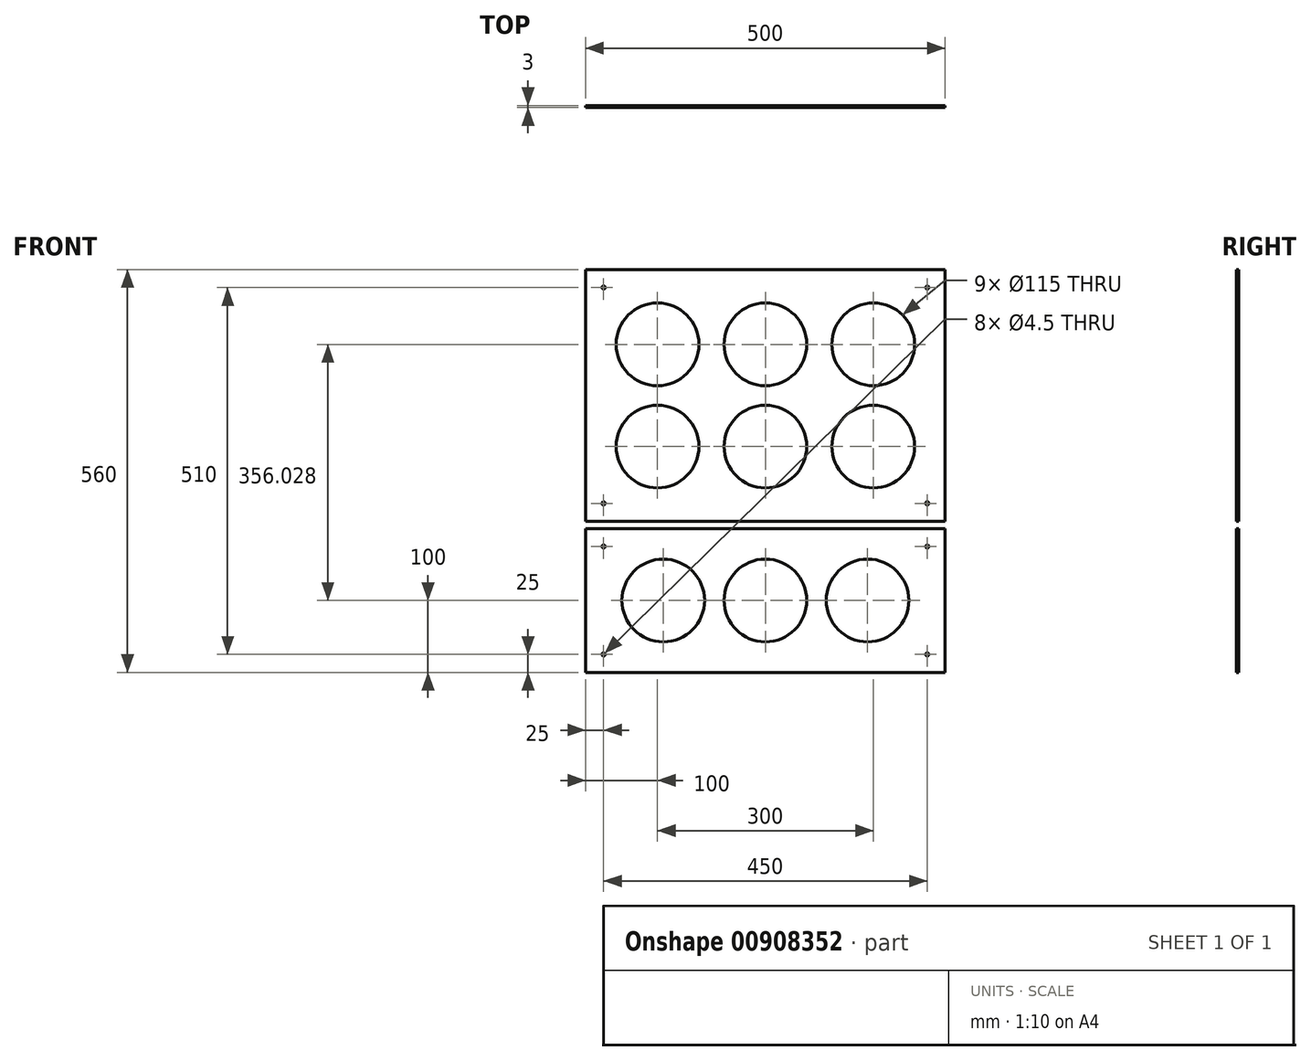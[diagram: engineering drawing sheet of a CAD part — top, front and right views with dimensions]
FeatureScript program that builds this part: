
annotation { "Feature Type Name" : "Feature", "Feature Type Description" : "" }
export const myFeature = defineFeature(function(context is Context, id is Id, definition is map)
    precondition{}
    {
        {
            var Q0;
            Q0=qCreatedBy(makeId("Front.planeOp"),FACE);
            var sketch = newSketch(context, id + "F0", { "sketchPlane" : qUnion([Q0])});
            skLineSegment(sketch, "E0.bottom", {"start": v(250, -40) * mm, "end": v(-250, -40) * mm});
            skLineSegment(sketch, "E0.top", {"start": v(250, 310) * mm, "end": v(-250, 310) * mm});
            skLineSegment(sketch, "E0.left", {"start": v(250, -40) * mm, "end": v(250, 310) * mm});
            skLineSegment(sketch, "E0.right", {"start": v(-250, -40) * mm, "end": v(-250, 310) * mm});
            skPoint(sketch, "E0.middle", {"position": v(0, 135) * mm});
            skLineSegment(sketch, "E1.bottom", {"start": v(250, -250) * mm, "end": v(-250, -250) * mm});
            skLineSegment(sketch, "E1.top", {"start": v(250, -50) * mm, "end": v(-250, -50) * mm});
            skLineSegment(sketch, "E1.left", {"start": v(250, -250) * mm, "end": v(250, -50) * mm});
            skLineSegment(sketch, "E1.right", {"start": v(-250, -250) * mm, "end": v(-250, -50) * mm});
            skPoint(sketch, "E1.middle", {"position": v(0, -150) * mm});
            skLineSegment(sketch, "E2.bottom", {"start": v(150, 63.97) * mm, "end": v(-150, 63.97) * mm, "construction": true});
            skLineSegment(sketch, "E2.top", {"start": v(150, 206.03) * mm, "end": v(-150, 206.03) * mm, "construction": true});
            skLineSegment(sketch, "E2.left", {"start": v(150, 63.97) * mm, "end": v(150, 206.03) * mm, "construction": true});
            skLineSegment(sketch, "E2.right", {"start": v(-150, 63.97) * mm, "end": v(-150, 206.03) * mm, "construction": true});
            skLineSegment(sketch, "E3.bottom", {"start": v(225, -225) * mm, "end": v(-225, -225) * mm, "construction": true});
            skLineSegment(sketch, "E3.top", {"start": v(225, -75) * mm, "end": v(-225, -75) * mm, "construction": true});
            skLineSegment(sketch, "E3.left", {"start": v(225, -225) * mm, "end": v(225, -75) * mm, "construction": true});
            skLineSegment(sketch, "E3.right", {"start": v(-225, -225) * mm, "end": v(-225, -75) * mm, "construction": true});
            skLineSegment(sketch, "E4", {"start": v(-142.06, -150) * mm, "end": v(142.06, -150) * mm, "construction": true});
            skCircle(sketch, "E5", {"center": v(142.06, -150) * mm, "radius": 57.5 * mm});
            skCircle(sketch, "E6", {"center": v(0, -150) * mm, "radius": 57.5 * mm});
            skCircle(sketch, "E7", {"center": v(-142.06, -150) * mm, "radius": 57.5 * mm});
            skLineSegment(sketch, "E8.bottom", {"start": v(225, -15) * mm, "end": v(-225, -15) * mm, "construction": true});
            skLineSegment(sketch, "E8.top", {"start": v(225, 285) * mm, "end": v(-225, 285) * mm, "construction": true});
            skLineSegment(sketch, "E8.left", {"start": v(225, -15) * mm, "end": v(225, 285) * mm, "construction": true});
            skLineSegment(sketch, "E8.right", {"start": v(-225, -15) * mm, "end": v(-225, 285) * mm, "construction": true});
            skLineSegment(sketch, "E9", {"start": v(0, 206.03) * mm, "end": v(0, 63.97) * mm, "construction": true});
            skCircle(sketch, "E10", {"center": v(150, 206.03) * mm, "radius": 57.5 * mm});
            skCircle(sketch, "E11", {"center": v(0, 206.03) * mm, "radius": 57.5 * mm});
            skCircle(sketch, "E12", {"center": v(-150, 206.03) * mm, "radius": 57.5 * mm});
            skCircle(sketch, "E13", {"center": v(-150, 63.97) * mm, "radius": 57.5 * mm});
            skCircle(sketch, "E14", {"center": v(0, 63.97) * mm, "radius": 57.5 * mm});
            skCircle(sketch, "E15", {"center": v(150, 63.97) * mm, "radius": 57.5 * mm});
            skSolve(sketch);
        }
        {
            var Q0;
            Q0=makeQuery(id+"F0.imprint","IMPRINT",FACE,{"disambiguationData":[TD([[makeQuery(id+"F0.imprint","IMPRINT",EDGE,{"derivedFrom":sQuery(id+"F0.wireOp",EDGE,"E1.bottom")}),-1.0]])]});
            var Q1;
            Q1=makeQuery(id+"F0.imprint","IMPRINT",FACE,{"disambiguationData":[TD([[makeQuery(id+"F0.imprint","IMPRINT",EDGE,{"derivedFrom":sQuery(id+"F0.wireOp",EDGE,"E0.bottom")}),-1.0]])]});
            var Q2;
            {var subQ5=sQuery(id+"F0.wireOp",EDGE,"E15");var subQ10=sQuery(id+"F0.wireOp",EDGE,"E2.bottom");var subQ15=makeQuery(id+"F0.imprint","INTERSECT",VERTEX,{"derivedFrom":[subQ10,subQ5]});Q2=makeQuery(id+"F0.imprint","IMPRINT",FACE,{"disambiguationData":[TD([[makeQuery(id+"F0.imprint","IMPRINT",EDGE,{"disambiguationData":[TD([[subQ15,-1.0]])],"derivedFrom":subQ10}),-1.0]])]});}
            var Q3;
            {var subQ11=sQuery(id+"F0.wireOp",EDGE,"E14");var subQ13=sQuery(id+"F0.wireOp",EDGE,"E2.bottom");var subQ14=makeQuery(id+"F0.imprint","INTERSECT",VERTEX,{"disambiguationData":[OD(1.0)],"derivedFrom":[subQ13,subQ11]});Q3=makeQuery(id+"F0.imprint","IMPRINT",FACE,{"disambiguationData":[TD([[makeQuery(id+"F0.imprint","IMPRINT",EDGE,{"disambiguationData":[TD([[subQ14,-1.0]])],"derivedFrom":subQ13}),-1.0]])]});}
            extrude(context, id + "F1", {"entities" : qUnion([Q0, Q1, Q2, Q3]), "depth" : 3 * mm, "offsetDistance" : 25 * mm});
        }
        {
            var Q0;
            Q0=sQuery(id+"F0.wireOp",VERTEX,"E8.top.start");
            var Q1;
            Q1=sQuery(id+"F0.wireOp",VERTEX,"E8.bottom.start");
            var Q2;
            Q2=sQuery(id+"F0.wireOp",VERTEX,"E8.bottom.end");
            var Q3;
            Q3=sQuery(id+"F0.wireOp",VERTEX,"E8.top.end");
            var Q4;
            Q4=sQuery(id+"F0.wireOp",VERTEX,"E3.bottom.end");
            var Q5;
            Q5=sQuery(id+"F0.wireOp",VERTEX,"E3.top.end");
            var Q6;
            Q6=sQuery(id+"F0.wireOp",VERTEX,"E3.top.start");
            var Q7;
            Q7=sQuery(id+"F0.wireOp",VERTEX,"E3.bottom.start");
            var Q8;
            Q8=makeQuery(id+"F1.opExtrude","SWEPT_BODY",BODY,{"disambiguationData":[OSD([sQuery(id+"F0.wireOp",EDGE,"E0.bottom"),sQuery(id+"F0.wireOp",EDGE,"E0.top"),sQuery(id+"F0.wireOp",EDGE,"E0.left"),sQuery(id+"F0.wireOp",EDGE,"E0.right"),sQuery(id+"F0.wireOp",EDGE,"E10"),sQuery(id+"F0.wireOp",EDGE,"E11"),sQuery(id+"F0.wireOp",EDGE,"E12"),sQuery(id+"F0.wireOp",EDGE,"E13"),sQuery(id+"F0.wireOp",EDGE,"E14"),sQuery(id+"F0.wireOp",EDGE,"E15")])]});
            var Q9;
            Q9=makeQuery(id+"F1.opExtrude","SWEPT_BODY",BODY,{"disambiguationData":[OSD([sQuery(id+"F0.wireOp",EDGE,"E1.bottom"),sQuery(id+"F0.wireOp",EDGE,"E1.top"),sQuery(id+"F0.wireOp",EDGE,"E1.left"),sQuery(id+"F0.wireOp",EDGE,"E1.right"),sQuery(id+"F0.wireOp",EDGE,"E5"),sQuery(id+"F0.wireOp",EDGE,"E6"),sQuery(id+"F0.wireOp",EDGE,"E7")])]});
            hole(context, id + "F2", {"style" : HoleStyle.SIMPLE, "endStyle" : HoleEndStyle.BLIND, "oppositeDirection" : true, "standardTappedOrClearance" : lookupTablePath({ "fit" : "Normal", "standard" : "ISO", "size" : "M4", "type" : "Clearance" }), "standardBlindInLast" : lookupTablePath({ "fit" : "Normal", "standard" : "ISO", "engagement" : "75%", "pitch" : "0.7 mm", "size" : "M4", "type" : "Clearance & tapped" }), "holeDiameter" : 4.5 * mm, "majorDiameter" : 5 * mm, "holeDepth" : 16.5 * mm, "isTappedThrough" : true, "tappedDepth" : 12 * mm, "tapClearance" : 3, "locations" : qUnion([Q0, Q1, Q2, Q3, Q4, Q5, Q6, Q7]), "scope" : qUnion([Q8, Q9])});
        }
    });
